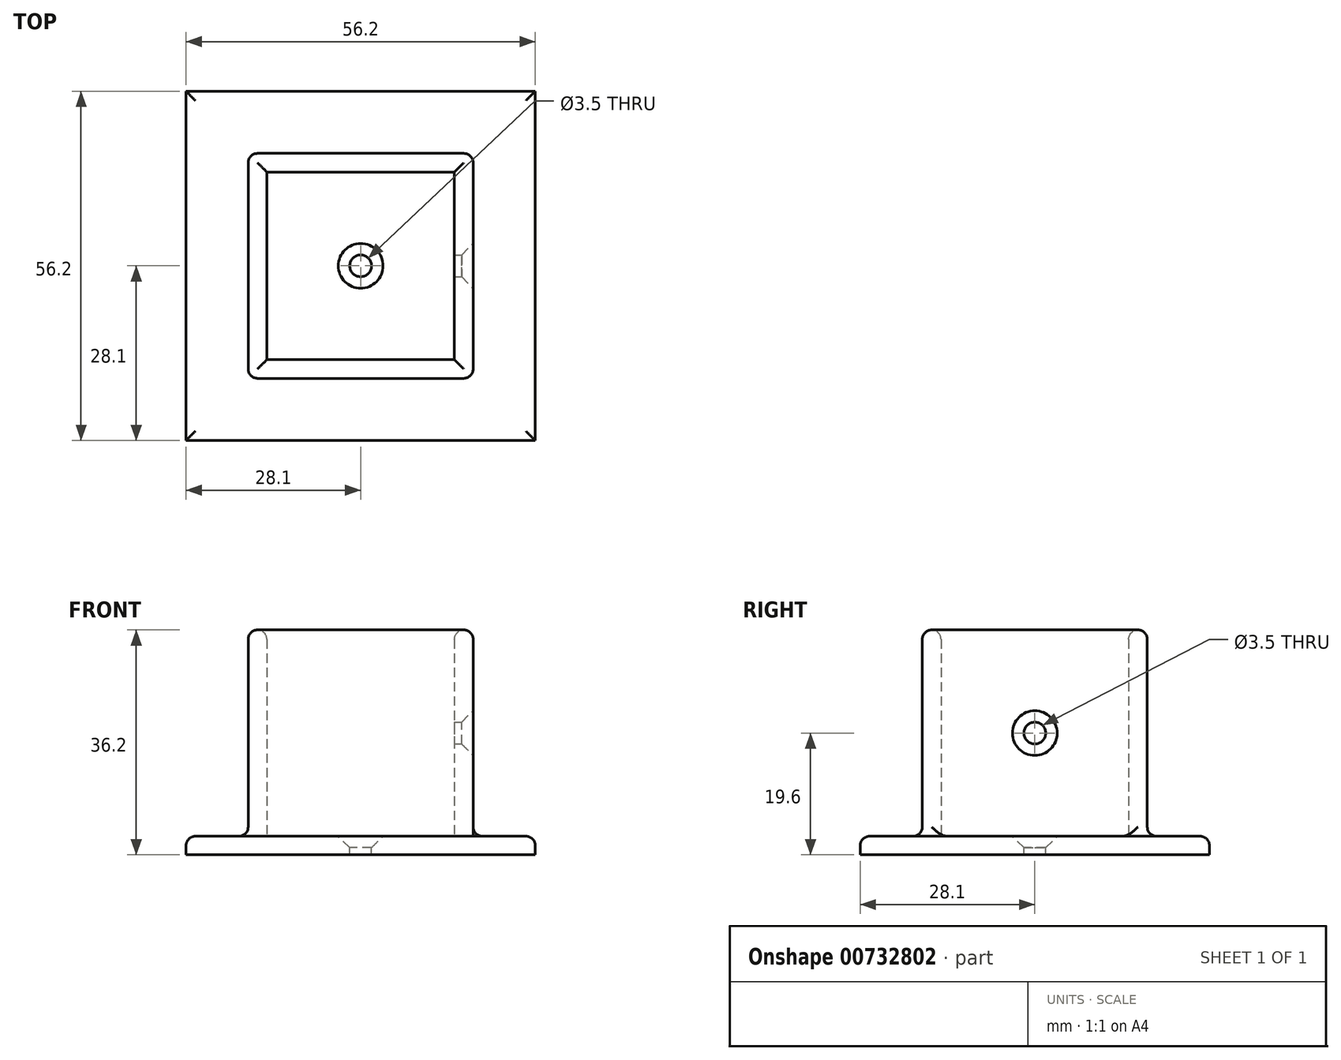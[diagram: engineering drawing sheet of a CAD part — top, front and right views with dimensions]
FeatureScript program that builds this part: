
annotation { "Feature Type Name" : "Feature", "Feature Type Description" : "" }
export const myFeature = defineFeature(function(context is Context, id is Id, definition is map)
    precondition{}
    {
        {
            var Q0;
            Q0=qCreatedBy(makeId("Top.planeOp"),FACE);
            var sketch = newSketch(context, id + "F0", { "sketchPlane" : qUnion([Q0])});
            skLineSegment(sketch, "E0.0", {"start": v(46.2, -10) * mm, "end": v(46.2, 46.2) * mm});
            skLineSegment(sketch, "E0.1", {"start": v(-10, -10) * mm, "end": v(46.2, -10) * mm});
            skLineSegment(sketch, "E0.2", {"start": v(-10, -10) * mm, "end": v(-10, 46.2) * mm});
            skLineSegment(sketch, "E0.3", {"start": v(-10, 46.2) * mm, "end": v(46.2, 46.2) * mm});
            skSolve(sketch);
        }
        {
            var Q0;
            Q0 = qSketchRegion(id + "F0", true);
            var Q1;
            Q1=makeQuery(id+"F0.imprint","IMPRINT",FACE,{"disambiguationData":[TD([[makeQuery(id+"F0.imprint","IMPRINT",EDGE,{"derivedFrom":sQuery(id+"F0.wireOp",EDGE,"waTLMGaw-IUor-W8n6-wlCW-p2pOx0xOtQnG.bottom")}),1.0]])]});
            extrude(context, id + "F1", {"entities" : qUnion([Q0, Q1]), "depth" : 3 * mm, "offsetDistance" : 25 * mm});
        }
        {
            var Q0;
            Q0=makeQuery(id+"F1.opExtrude","CAP_FACE",FACE,{"disambiguationData":[OSD([sQuery(id+"F0.wireOp",EDGE,"E0.0"),sQuery(id+"F0.wireOp",EDGE,"E0.1"),sQuery(id+"F0.wireOp",EDGE,"E0.2"),sQuery(id+"F0.wireOp",EDGE,"E0.3")])],"isStart":false});
            var sketch = newSketch(context, id + "F2", { "sketchPlane" : qUnion([Q0])});
            skLineSegment(sketch, "E1.bottom", {"start": v(-10, -10) * mm, "end": v(46.2, -10) * mm});
            skLineSegment(sketch, "E1.top", {"start": v(-10, 46.2) * mm, "end": v(46.2, 46.2) * mm});
            skLineSegment(sketch, "E1.left", {"start": v(-10, -10) * mm, "end": v(-10, 46.2) * mm});
            skLineSegment(sketch, "E1.right", {"start": v(46.2, -10) * mm, "end": v(46.2, 46.2) * mm});
            skLineSegment(sketch, "E2.0", {"start": v(0, 36.2) * mm, "end": v(36.2, 36.2) * mm});
            skLineSegment(sketch, "E2.1", {"start": v(0, 0) * mm, "end": v(0, 36.2) * mm});
            skLineSegment(sketch, "E2.2", {"start": v(0, 0) * mm, "end": v(36.2, 0) * mm});
            skLineSegment(sketch, "E2.3", {"start": v(36.2, 0) * mm, "end": v(36.2, 36.2) * mm});
            skLineSegment(sketch, "E3.0", {"start": v(3, 33.2) * mm, "end": v(33.2, 33.2) * mm});
            skLineSegment(sketch, "E3.1", {"start": v(3, 3) * mm, "end": v(3, 33.2) * mm});
            skLineSegment(sketch, "E3.2", {"start": v(3, 3) * mm, "end": v(33.2, 3) * mm});
            skLineSegment(sketch, "E3.3", {"start": v(33.2, 3) * mm, "end": v(33.2, 33.2) * mm});
            skPoint(sketch, "E4", {"position": v(18.1, 18.1) * mm});
            skSolve(sketch);
        }
        {
            var Q0;
            Q0=makeQuery(id+"F2.imprint","IMPRINT",FACE,{"disambiguationData":[TD([[makeQuery(id+"F2.imprint","IMPRINT",EDGE,{"derivedFrom":sQuery(id+"F2.wireOp",EDGE,"E2.0")}),-1.0]])]});
            extrude(context, id + "F3", {"entities" : qUnion([Q0]), "operationType" : NewBodyOperationType.ADD, "depth" : 33.2 * mm, "offsetDistance" : 25 * mm});
        }
        {
            var Q0;
            Q0=sQuery(id+"F2.wireOp",VERTEX,"E4");
            var Q1;
            Q1=makeQuery(id+"F1.opExtrude","SWEPT_BODY",BODY,{"disambiguationData":[OSD([sQuery(id+"F0.wireOp",EDGE,"E0.0"),sQuery(id+"F0.wireOp",EDGE,"E0.1"),sQuery(id+"F0.wireOp",EDGE,"E0.2"),sQuery(id+"F0.wireOp",EDGE,"E0.3")])]});
            hole(context, id + "F4", {"style" : HoleStyle.C_SINK, "endStyle" : HoleEndStyle.BLIND, "holeDiameter" : 3.5 * mm, "cSinkDiameter" : 7.2 * mm, "cSinkAngle" : 90 * degree, "majorDiameter" : 5 * mm, "holeDepth" : 13.5 * mm, "isTappedThrough" : true, "tappedDepth" : 12 * mm, "tapClearance" : 3, "startFromSketch" : true, "locations" : qUnion([Q0]), "scope" : qUnion([Q1])});
        }
        {
            var Q0;
            Q0=makeQuery(id+"F3.opExtrude","CAP_EDGE",EDGE,{"disambiguationData":[OSD([sQuery(id+"F2.wireOp",EDGE,"E3.3")])],"isStart":false});
            var Q1;
            Q1=makeQuery(id+"F3.opExtrude","CAP_EDGE",EDGE,{"disambiguationData":[OSD([sQuery(id+"F2.wireOp",EDGE,"E3.2")])],"isStart":false});
            var Q2;
            Q2=makeQuery(id+"F3.opExtrude","CAP_EDGE",EDGE,{"disambiguationData":[OSD([sQuery(id+"F2.wireOp",EDGE,"E2.2")])],"isStart":true});
            var Q3;
            Q3=makeQuery(id+"F3.opExtrude","CAP_EDGE",EDGE,{"disambiguationData":[OSD([sQuery(id+"F2.wireOp",EDGE,"E3.0")])],"isStart":false});
            var Q4;
            Q4=makeQuery(id+"F3.opExtrude","CAP_EDGE",EDGE,{"disambiguationData":[OSD([sQuery(id+"F2.wireOp",EDGE,"E3.1")])],"isStart":false});
            var Q5;
            Q5=makeQuery(id+"F3.opExtrude","CAP_EDGE",EDGE,{"disambiguationData":[OSD([sQuery(id+"F2.wireOp",EDGE,"E2.1")])],"isStart":false});
            var Q6;
            Q6=makeQuery(id+"F3.opExtrude","CAP_EDGE",EDGE,{"disambiguationData":[OSD([sQuery(id+"F2.wireOp",EDGE,"E2.0")])],"isStart":false});
            var Q7;
            Q7=makeQuery(id+"F3.opExtrude","CAP_EDGE",EDGE,{"disambiguationData":[OSD([sQuery(id+"F2.wireOp",EDGE,"E2.3")])],"isStart":false});
            var Q8;
            Q8=makeQuery(id+"F3.opExtrude","CAP_EDGE",EDGE,{"disambiguationData":[OSD([sQuery(id+"F2.wireOp",EDGE,"E2.2")])],"isStart":false});
            var Q9;
            Q9=makeQuery(id+"F3.opExtrude","SWEPT_EDGE",EDGE,{"disambiguationData":[OSD([sQuery(id+"F2.wireOp",EDGE,"E2.2"),sQuery(id+"F2.wireOp",EDGE,"E2.3")])]});
            var Q10;
            Q10=makeQuery(id+"F3.opExtrude","SWEPT_EDGE",EDGE,{"disambiguationData":[OSD([sQuery(id+"F2.wireOp",EDGE,"E2.1"),sQuery(id+"F2.wireOp",EDGE,"E2.2")])]});
            var Q11;
            Q11=makeQuery(id+"F3.opExtrude","CAP_EDGE",EDGE,{"disambiguationData":[OSD([sQuery(id+"F2.wireOp",EDGE,"E2.1")])],"isStart":true});
            var Q12;
            Q12=makeQuery(id+"F3.opExtrude","CAP_EDGE",EDGE,{"disambiguationData":[OSD([sQuery(id+"F2.wireOp",EDGE,"E2.0")])],"isStart":true});
            var Q13;
            Q13=makeQuery(id+"F3.opExtrude","SWEPT_EDGE",EDGE,{"disambiguationData":[OSD([sQuery(id+"F2.wireOp",EDGE,"E2.0"),sQuery(id+"F2.wireOp",EDGE,"E2.3")])]});
            var Q14;
            Q14=makeQuery(id+"F3.opExtrude","SWEPT_EDGE",EDGE,{"disambiguationData":[OSD([sQuery(id+"F2.wireOp",EDGE,"E2.0"),sQuery(id+"F2.wireOp",EDGE,"E2.1")])]});
            var Q15;
            Q15=makeQuery(id+"F1.opExtrude","CAP_EDGE",EDGE,{"disambiguationData":[OSD([sQuery(id+"F0.wireOp",EDGE,"E0.3")])],"isStart":false});
            var Q16;
            Q16=makeQuery(id+"F1.opExtrude","CAP_EDGE",EDGE,{"disambiguationData":[OSD([sQuery(id+"F0.wireOp",EDGE,"E0.2")])],"isStart":false});
            var Q17;
            Q17=makeQuery(id+"F1.opExtrude","CAP_EDGE",EDGE,{"disambiguationData":[OSD([sQuery(id+"F0.wireOp",EDGE,"E0.1")])],"isStart":false});
            var Q18;
            Q18=makeQuery(id+"F1.opExtrude","CAP_EDGE",EDGE,{"disambiguationData":[OSD([sQuery(id+"F0.wireOp",EDGE,"E0.0")])],"isStart":false});
            fillet(context, id + "F5", {"entities" : qUnion([Q0, Q1, Q2, Q3, Q4, Q5, Q6, Q7, Q8, Q9, Q10, Q11, Q12, Q13, Q14, Q15, Q16, Q17, Q18]), "radius" : 1.5 * mm, "tangentPropagation" : true, "allowEdgeOverflow" : false});
        }
        {
            var Q0;
            Q0=makeQuery(id+"F3.opExtrude","SWEPT_FACE",FACE,{"disambiguationData":[OSD([sQuery(id+"F2.wireOp",EDGE,"E2.3")])]});
            var sketch = newSketch(context, id + "F6", { "sketchPlane" : qUnion([Q0])});
            skPoint(sketch, "E5", {"position": v(18.1, 19.6) * mm});
            skSolve(sketch);
        }
        {
            var Q0;
            Q0=sQuery(id+"F6.wireOp",VERTEX,"E5");
            var Q1;
            Q1=makeQuery(id+"F1.opExtrude","SWEPT_BODY",BODY,{"disambiguationData":[OSD([sQuery(id+"F0.wireOp",EDGE,"E0.0"),sQuery(id+"F0.wireOp",EDGE,"E0.1"),sQuery(id+"F0.wireOp",EDGE,"E0.2"),sQuery(id+"F0.wireOp",EDGE,"E0.3")])]});
            hole(context, id + "F7", {"style" : HoleStyle.C_SINK, "endStyle" : HoleEndStyle.BLIND, "holeDiameter" : 3.5 * mm, "cSinkDiameter" : 7.2 * mm, "cSinkAngle" : 90 * degree, "majorDiameter" : 5 * mm, "holeDepth" : 13.5 * mm, "isTappedThrough" : true, "tappedDepth" : 12 * mm, "tapClearance" : 3, "startFromSketch" : true, "locations" : qUnion([Q0]), "scope" : qUnion([Q1])});
        }
    });
